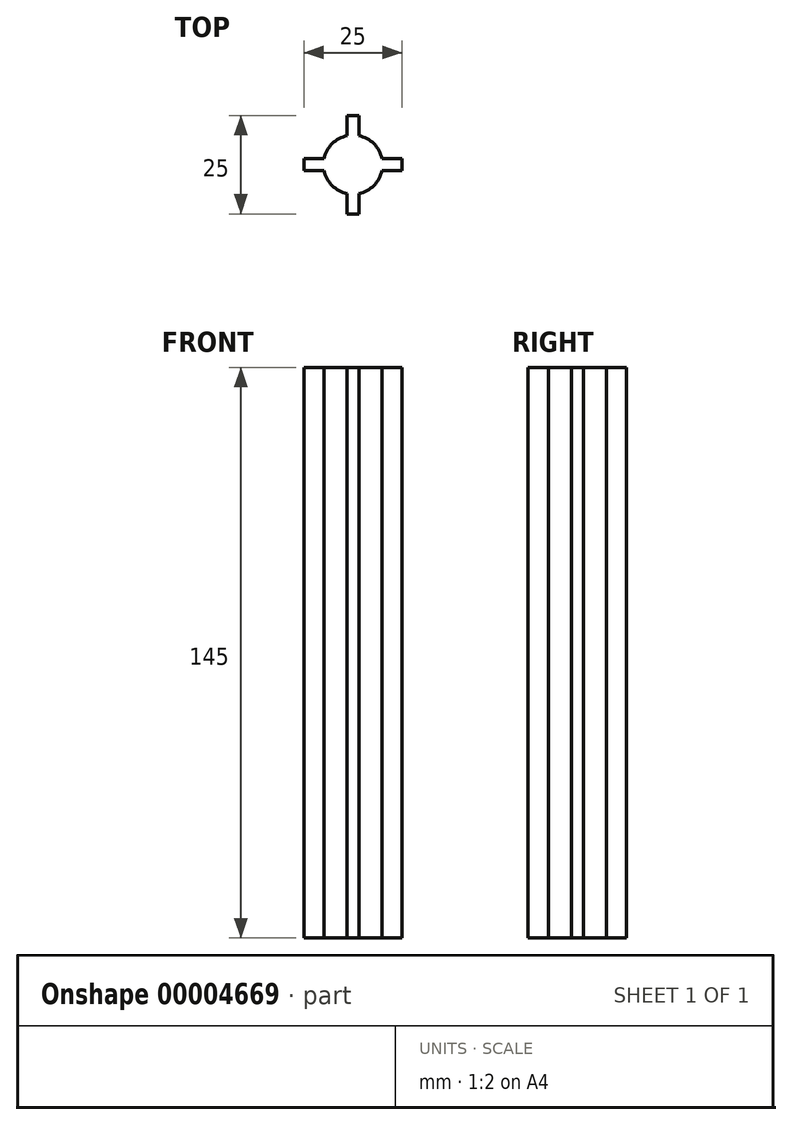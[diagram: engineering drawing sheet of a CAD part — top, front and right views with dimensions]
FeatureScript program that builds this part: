
annotation { "Feature Type Name" : "Feature", "Feature Type Description" : "" }
export const myFeature = defineFeature(function(context is Context, id is Id, definition is map)
    precondition{}
    {
        {
            var Q0;
            Q0=qCreatedBy(makeId("Top.planeOp"),FACE);
            var sketch = newSketch(context, id + "F0", { "sketchPlane" : qUnion([Q0])});
            skArc(sketch, "E0", {"start": v(-1.5, 7.35) * mm, "mid": v(-5.3, 5.3) * mm, "end": v(-7.35, 1.5) * mm});
            skLineSegment(sketch, "E1.rect.bottom", {"start": v(1.5, 12.5) * mm, "end": v(-1.5, 12.5) * mm});
            skLineSegment(sketch, "E1.rect.top", {"start": v(1.5, -12.5) * mm, "end": v(-1.5, -12.5) * mm});
            skLineSegment(sketch, "E1.rect.left", {"start": v(1.5, 12.5) * mm, "end": v(1.5, 7.35) * mm});
            skLineSegment(sketch, "E1.rect.right", {"start": v(-1.5, 12.5) * mm, "end": v(-1.5, 7.35) * mm});
            skLineSegment(sketch, "E2.rect.bottom", {"start": v(12.5, -1.5) * mm, "end": v(7.35, -1.5) * mm});
            skLineSegment(sketch, "E2.rect.top", {"start": v(12.5, 1.5) * mm, "end": v(7.35, 1.5) * mm});
            skLineSegment(sketch, "E2.rect.left", {"start": v(12.5, -1.5) * mm, "end": v(12.5, 1.5) * mm});
            skLineSegment(sketch, "E2.rect.right", {"start": v(-12.5, -1.5) * mm, "end": v(-12.5, 1.5) * mm});
            skLineSegment(sketch, "E3.trimOffspring", {"start": v(-1.5, -7.35) * mm, "end": v(-1.5, -12.5) * mm});
            skArc(sketch, "E4.trimOffspring", {"start": v(-7.35, -1.5) * mm, "mid": v(-5.3, -5.3) * mm, "end": v(-1.5, -7.35) * mm});
            skLineSegment(sketch, "E5.trimOffspring", {"start": v(-7.35, -1.5) * mm, "end": v(-12.5, -1.5) * mm});
            skLineSegment(sketch, "E6.trimOffspring", {"start": v(1.5, -7.35) * mm, "end": v(1.5, -12.5) * mm});
            skLineSegment(sketch, "E7.trimOffspring", {"start": v(-7.35, 1.5) * mm, "end": v(-12.5, 1.5) * mm});
            skArc(sketch, "E8.trimOffspring", {"start": v(7.35, 1.5) * mm, "mid": v(5.3, 5.3) * mm, "end": v(1.5, 7.35) * mm});
            skArc(sketch, "E9.trimOffspring", {"start": v(1.5, -7.35) * mm, "mid": v(5.3, -5.3) * mm, "end": v(7.35, -1.5) * mm});
            skSolve(sketch);
        }
        {
            var Q0;
            Q0=makeQuery(id+"F0.imprint","IMPRINT",FACE,{"disambiguationData":[TD([[makeQuery(id+"F0.imprint","IMPRINT",EDGE,{"derivedFrom":sQuery(id+"F0.wireOp",EDGE,"E0")}),1.0]])]});
            extrude(context, id + "F1", {"entities" : qUnion([Q0]), "depth" : 145 * mm});
        }
    });
